# Revit family: RFA2 4070T_Pocket
name_source: partatom
category: Doors
revit_build: Autodesk Revit 2016 (Build: 20170117_1200(x64)
units: mm (PartAtom-declared; Revit-internal decimal feet)

## family parameters
Always vertical = Yes
Cut with Voids When Loaded = No
Host = Wall
OmniClass Number = 23.30.10.00
OmniClass Title = Doors
Room Calculation Point = No
Shared = No

## types (1)
- RFA2 4070T_Pocket
    A = 0' - 1 13/32"
    Actuator Height = 4' - 0"
    B = 0' - 0 1/16"
    Bigger Number = 2
    Delete = 0' - 0 11/16"
    Depth = 0' - 5 3/4"
    Depth1 = 0' - 6 5/32"
    Function = Interior
    Height = 6' - 10 5/16"
    Net Frame Height = 7' - 0"
    Net Frame Width = 8' - 0"
    Panel Left1 = 1
    Panel_Single Width = 7' - 11 5/16"
    Panels = 3
    Panels Left = 1
    Panels Material = Alluminium
    Panels_Both Side Pocket = 3
    Panels_Single Pocket = 3
    Phantom_Left = Yes
    Pocket = Yes
    Pocket Both Sides = No
    Pocket Depth Left = 0' - 3 5/8"
    Pocket Depth Right = 0' - 6 1/2"
    Pocket Width Left = 2' - 0"
    Pocket Width Left_Both = 0' - 0"
    Pocket Width Left_Single = 2' - 7 25/32"
    Pocket Width Right = 3' - 0"
    Pocket Width Right1 = 0' - 0"
    Right Panel = 2
    Shims = 0' - 0 1/4"
    Single Depth = 0' - 9 3/8"
    Single Panel = 0' - 2 7/8"
    Single Panel Half = 0' - 1 7/16"
    Single Panel Width = 2' - 7 25/32"
    Wall Closure = By host
    Width = 8' - 0 1/2"

## geometry (parser evidence)
native form markers: Sweep x41
no freeform markers — native parametric forms only
